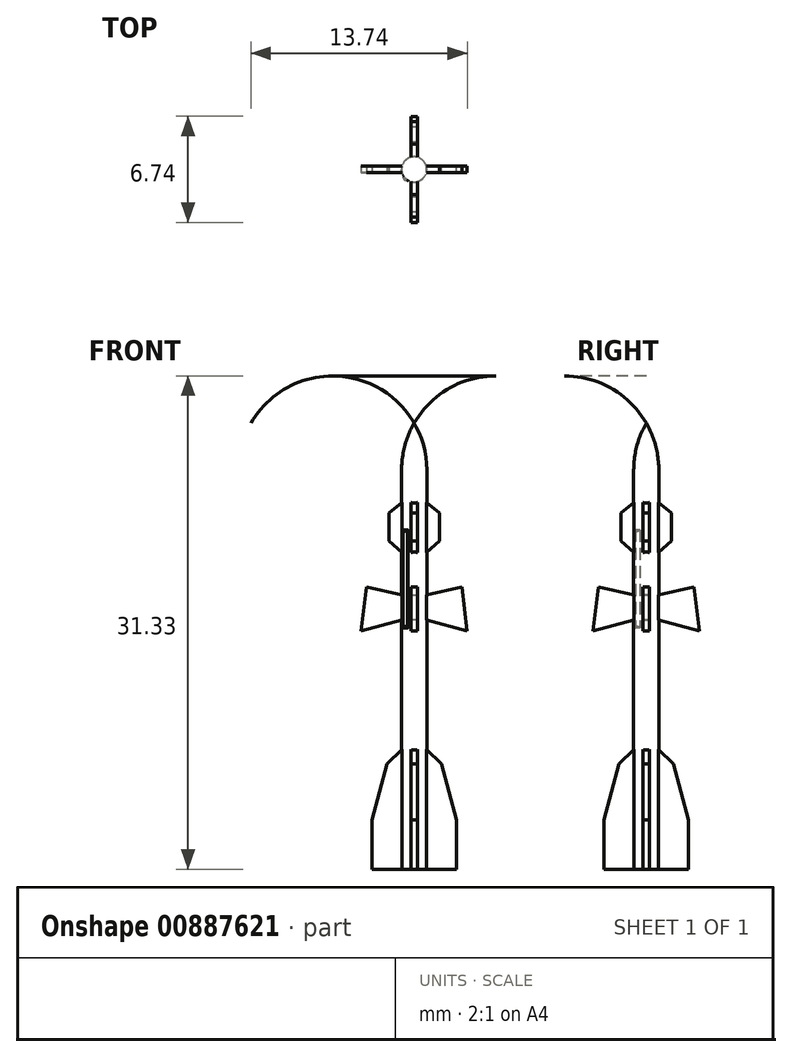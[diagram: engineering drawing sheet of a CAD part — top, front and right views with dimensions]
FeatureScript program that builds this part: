
annotation { "Feature Type Name" : "Feature", "Feature Type Description" : "" }
export const myFeature = defineFeature(function(context is Context, id is Id, definition is map)
    precondition{}
    {
        {
            assignVariable(context, id + "F0", {"name" : "s", "anyValue" : 144});
        }
        {
            var Q0;
            Q0=qCreatedBy(makeId("Front.planeOp"),FACE);
            var sketch = newSketch(context, id + "F1", { "sketchPlane" : qUnion([Q0])});
            skLineSegment(sketch, "E0", {"start": v(0, 0) * mm, "end": v(0, 28.33) * mm});
            skLineSegment(sketch, "E1", {"start": v(0.8, 25.35) * mm, "end": v(0.8, 0) * mm});
            skLineSegment(sketch, "E2", {"start": v(0.8, 0) * mm, "end": v(0, 0) * mm});
            skArc(sketch, "E3", {"start": v(0.8, 25.35) * mm, "mid": v(0.6, 26.9) * mm, "end": v(0, 28.33) * mm});
            skSolve(sketch);
        }
        {
            var Q0;
            Q0=qSketchRegion(id+"F1",true);
            var Q1;
            Q1=sQuery(id+"F1.wireOp",EDGE,"E0");
            revolve(context, id + "F2", {"surfaceOperationType" : NewSurfaceOperationType.NEW, "entities" : qUnion([Q0]), "axis" : qUnion([Q1]), "revolveType" : RevolveType.FULL});
        }
        {
            var Q0;
            Q0=qCreatedBy(makeId("Front.planeOp"),FACE);
            var sketch = newSketch(context, id + "F3", { "sketchPlane" : qUnion([Q0])});
            skLineSegment(sketch, "E4", {"start": v(0, 0) * mm, "end": v(0, 23.89) * mm});
            skLineSegment(sketch, "E5", {"start": v(0, 23.89) * mm, "end": v(1.6, 22.64) * mm});
            skLineSegment(sketch, "E6", {"start": v(1.6, 22.64) * mm, "end": v(1.6, 20.83) * mm});
            skLineSegment(sketch, "E7", {"start": v(1.6, 20.83) * mm, "end": v(0.4, 19.8) * mm});
            skLineSegment(sketch, "E8", {"start": v(0.4, 19.8) * mm, "end": v(0.4, 17.34) * mm});
            skLineSegment(sketch, "E9", {"start": v(0.4, 17.34) * mm, "end": v(3.02, 17.92) * mm});
            skLineSegment(sketch, "E10", {"start": v(3.02, 17.92) * mm, "end": v(3.37, 15.14) * mm});
            skLineSegment(sketch, "E11", {"start": v(3.37, 15.14) * mm, "end": v(0.4, 15.94) * mm});
            skLineSegment(sketch, "E12", {"start": v(0.4, 15.94) * mm, "end": v(0.4, 7.94) * mm});
            skLineSegment(sketch, "E13", {"start": v(0.4, 7.94) * mm, "end": v(1.74, 6.7) * mm});
            skLineSegment(sketch, "E14", {"start": v(1.74, 6.7) * mm, "end": v(2.67, 3.12) * mm});
            skLineSegment(sketch, "E15", {"start": v(2.67, 3.12) * mm, "end": v(2.67, 0) * mm});
            skLineSegment(sketch, "E16", {"start": v(2.67, 0) * mm, "end": v(0, 0) * mm});
            skLineSegment(sketch, "E17.0", {"start": v(0.8, 0) * mm, "end": v(-0.8, 0) * mm});
            skLineSegment(sketch, "E18", {"start": v(0.8, 0) * mm, "end": v(0.8, 32.87) * mm, "construction": true});
            skPoint(sketch, "E19", {"position": v(0.8, 7.57) * mm});
            skPoint(sketch, "E20", {"position": v(0.8, 15.83) * mm});
            skPoint(sketch, "E21", {"position": v(0.8, 17.43) * mm});
            skPoint(sketch, "E22", {"position": v(0.8, 20.14) * mm});
            skPoint(sketch, "E23", {"position": v(0.8, 23.26) * mm});
            skSolve(sketch);
        }
        {
            var Q0;
            Q0=qSketchRegion(id+"F3",true);
            extrude(context, id + "F4", {"entities" : qUnion([Q0]), "operationType" : NewBodyOperationType.ADD, "depth" : .4 * mm, "offsetDistance" : 25 * mm, "symmetric" : true});
        }
        {
            var Q0;
            Q0=makeQuery(id+"F2.opRevolve","SWEPT_BODY",BODY,{"disambiguationData":[OSD([sQuery(id+"F1.wireOp",EDGE,"E0"),sQuery(id+"F1.wireOp",EDGE,"E1"),sQuery(id+"F1.wireOp",EDGE,"E2"),sQuery(id+"F1.wireOp",EDGE,"2EiOItwe-9FNA-eY8p-DkXH-AMy5AHyUmzZA"),sQuery(id+"F1.wireOp",EDGE,"E3")])]});
            var Q1;
            Q1=makeQuery(id+"F2.opRevolve","SWEPT_FACE",FACE,{"disambiguationData":[OSD([sQuery(id+"F1.wireOp",EDGE,"E1")])]});
            circularPattern(context, id + "F5", {"operationType" : NewBodyOperationType.ADD, "entities" : qUnion([Q0]), "axis" : qUnion([Q1]), "angle" : 360 * degree, "instanceCount" : 4, "equalSpace" : true, "computeTransformsWithoutBuiltin" : true});
        }
        {
            var Q0;
            Q0=qCreatedBy(makeId("Top.planeOp"),FACE);
            cPlane(context, id + "F6", {"entities" : qUnion([Q0]), "cplaneType" : CPlaneType.OFFSET, "offset" : (2220 / getVariable(context, 's')) * mm, "width" : 150 * mm, "height" : 150 * mm});
        }
        {
            var Q0;
            Q0=qCreatedBy(id+"F6.planeOp",FACE);
            var sketch = newSketch(context, id + "F7", { "sketchPlane" : qUnion([Q0])});
            skLineSegment(sketch, "E24", {"start": v(-0.14, -0.44) * mm, "end": v(-0.44, -0.14) * mm});
            skLineSegment(sketch, "E25", {"start": v(-0.44, -0.14) * mm, "end": v(-0.7, -0.4) * mm});
            skLineSegment(sketch, "E26", {"start": v(-0.4, -0.7) * mm, "end": v(-0.14, -0.44) * mm});
            skLineSegment(sketch, "E27", {"start": v(0, -0.64) * mm, "end": v(0, 0) * mm, "construction": true});
            skLineSegment(sketch, "E28", {"start": v(0, 0) * mm, "end": v(-0.29, -0.29) * mm, "construction": true});
            skArc(sketch, "E29", {"start": v(-0.7, -0.4) * mm, "mid": v(-0.64, -0.64) * mm, "end": v(-0.4, -0.7) * mm});
            skSolve(sketch);
        }
        {
            var Q0;
            Q0=qSketchRegion(id+"F7",true);
            extrude(context, id + "F8", {"entities" : qUnion([Q0]), "operationType" : NewBodyOperationType.ADD, "depth" : (870 / getVariable(context, 's')) * mm, "offsetDistance" : 25 * mm});
        }
        {
            var Q0;
            Q0=makeQuery(id+"F8.boolean.opBoolean","INTERSECT",EDGE,{"derivedFrom":[makeQuery(id+"F2.opRevolve","SWEPT_FACE",FACE,{"disambiguationData":[OSD([sQuery(id+"F1.wireOp",EDGE,"E1")])]}),makeQuery(id+"F8.opExtrude","CAP_FACE",FACE,{"disambiguationData":[OSD([sQuery(id+"F7.wireOp",EDGE,"E24"),sQuery(id+"F7.wireOp",EDGE,"E25"),sQuery(id+"F7.wireOp",EDGE,"E26"),sQuery(id+"F7.wireOp",EDGE,"E29")])],"isStart":false})]});
            var Q1;
            Q1=makeQuery(id+"F8.boolean.opBoolean","INTERSECT",EDGE,{"derivedFrom":[makeQuery(id+"F2.opRevolve","SWEPT_FACE",FACE,{"disambiguationData":[OSD([sQuery(id+"F1.wireOp",EDGE,"E1")])]}),makeQuery(id+"F8.opExtrude","CAP_FACE",FACE,{"disambiguationData":[OSD([sQuery(id+"F7.wireOp",EDGE,"E24"),sQuery(id+"F7.wireOp",EDGE,"E25"),sQuery(id+"F7.wireOp",EDGE,"E26"),sQuery(id+"F7.wireOp",EDGE,"E29")])],"isStart":true})]});
            chamfer(context, id + "F9", {"entities" : qUnion([Q0, Q1]), "width" : .1 * mm, "tangentPropagation" : true});
        }
    });
